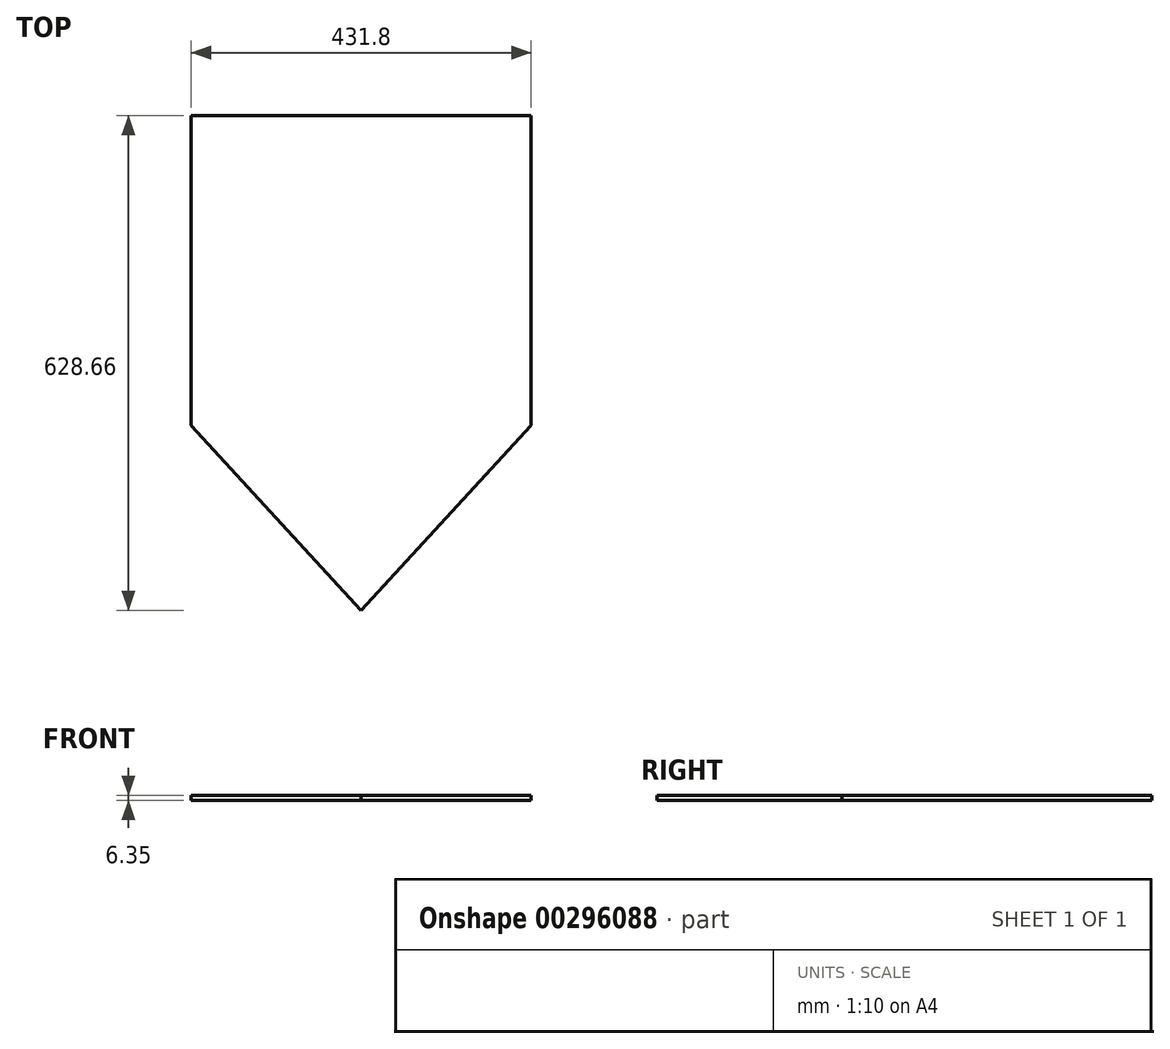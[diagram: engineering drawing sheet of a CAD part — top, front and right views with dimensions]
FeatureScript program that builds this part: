
annotation { "Feature Type Name" : "Feature", "Feature Type Description" : "" }
export const myFeature = defineFeature(function(context is Context, id is Id, definition is map)
    precondition{}
    {
        {
            var Q0;
            Q0=qCreatedBy(makeId("Top.planeOp"),FACE);
            var sketch = newSketch(context, id + "F0", { "sketchPlane" : qUnion([Q0])});
            skLineSegment(sketch, "E0", {"start": v(-215.9, 314.33) * mm, "end": v(215.9, 314.33) * mm});
            skLineSegment(sketch, "E1", {"start": v(215.9, 314.33) * mm, "end": v(215.9, -79.37) * mm});
            skLineSegment(sketch, "E2", {"start": v(215.9, -79.37) * mm, "end": v(0, -314.33) * mm});
            skLineSegment(sketch, "E3", {"start": v(0, -314.33) * mm, "end": v(-215.9, -79.37) * mm});
            skLineSegment(sketch, "E4", {"start": v(-215.9, -79.37) * mm, "end": v(-215.9, 314.33) * mm});
            skPoint(sketch, "E5", {"position": v(0, 314.33) * mm});
            skSolve(sketch);
        }
        {
            var Q0;
            Q0=makeQuery(id+"F0.imprint","IMPRINT",FACE,{"disambiguationData":[TD([[makeQuery(id+"F0.imprint","IMPRINT",EDGE,{"derivedFrom":sQuery(id+"F0.wireOp",EDGE,"E0")}),-1.0]])]});
            extrude(context, id + "F1", {"entities" : qUnion([Q0]), "depth" : 6.35 * mm});
        }
    });
